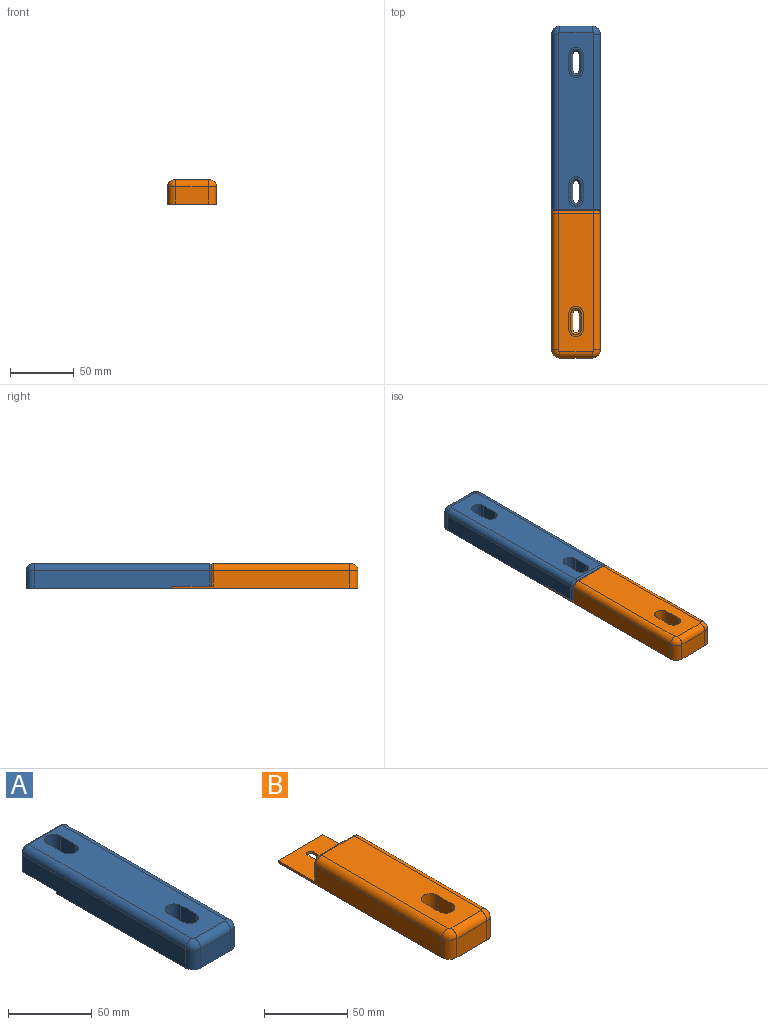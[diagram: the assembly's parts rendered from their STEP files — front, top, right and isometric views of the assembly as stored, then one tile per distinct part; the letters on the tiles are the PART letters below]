
ASSEMBLY  parts=2 mates=1
PART A: 42 faces, bbox 38.9x145.3x19.5 mm
  f0: plane 23.81x11.11mm, normal (0,0,1), area 87.8mm2, adj f16,f17,f18,f19,f26,f27,f28,f29
  f1: plane 137.32x13.97mm, normal (-1,0,0), area 1873mm2, adj f10,f11,f21,f22,f32,f41
  f2: plane 137.32x13.97mm, normal (1,0,0), area 1873mm2, adj f5,f11,f21,f22,f36,f37
  f3: plane 23.81x11.11mm, normal (0,0,1), area 87.8mm2, adj f12,f13,f14,f15,f23,f24,f25,f30
  f4: plane 25.4x13.97mm, normal (0,-1,0), area 354.8mm2, adj f5,f10,f11,f34
  f5: cylinder r=6.35mm len=13.97mm, axis (0,0,-1), area 139.3mm2, adj f2,f4,f11,f35
  f6: plane 12.7x1.59mm, normal (-1,0,0), area 20.2mm2, adj f7,f9,f11,f16
  f7: cylinder r=2.38mm len=4.76mm, axis (0,0,-1), area 11.9mm2, adj f6,f8,f11,f17
  f8: plane 12.7x1.59mm, normal (1,0,0), area 20.2mm2, adj f7,f9,f11,f19
  f9: cylinder r=2.38mm len=4.76mm, axis (0,0,-1), area 11.9mm2, adj f6,f8,f11,f18
  f10: cylinder r=6.35mm len=13.97mm, axis (0,0,-1), area 139.3mm2, adj f1,f4,f11,f33
  f11: plane 115.09x38.1mm, normal (0,0,-1), area 4289.5mm2, adj f1,f2,f4,f5,f6,f7,f8,f9
  f12: plane 12.7x1.59mm, normal (-0.71,0,0.71), area 28.5mm2, adj f3,f13,f14,f22
  f13: cone r=2.38mm half-angle=45deg, axis (0,0,1), area 22.4mm2, adj f3,f12,f15,f22
  f14: cone r=2.38mm half-angle=45deg, axis (0,0,1), area 22.4mm2, adj f3,f12,f15,f22
  f15: plane 12.7x1.59mm, normal (0.71,0,0.71), area 28.5mm2, adj f3,f13,f14,f22
  f16: plane 12.7x1.59mm, normal (-0.71,0,0.71), area 28.5mm2, adj f0,f6,f17,f18
  f17: cone r=2.38mm half-angle=45deg, axis (0,0,1), area 22.4mm2, adj f0,f7,f16,f19
  f18: cone r=2.38mm half-angle=45deg, axis (0,0,1), area 22.4mm2, adj f0,f9,f16,f19
  f19: plane 12.7x1.59mm, normal (0.71,0,0.71), area 28.5mm2, adj f0,f8,f17,f18
  f20: plane 34.93x15.88mm, normal (0,1,0), area 549.2mm2, adj f22,f37,f38,f39,f40,f41
  f21: plane 38.1x1.59mm, normal (0,1,0), area 60.5mm2, adj f1,f2,f11,f22
  f22: plane 38.1x30.16mm, normal (0,0,-1), area 1069.8mm2, adj f1,f2,f12,f13,f14,f15,f20,f21
  f23: cylinder r=5.56mm len=15.88mm, axis (0,0,-1), area 277.1mm2, adj f3,f24,f30,f31
  f24: plane 15.88x12.7mm, normal (-1,0,0), area 201.6mm2, adj f3,f23,f25,f31
  f25: cylinder r=5.56mm len=15.88mm, axis (0,0,-1), area 277.1mm2, adj f3,f24,f30,f31
  f26: cylinder r=5.56mm len=15.88mm, axis (0,0,-1), area 277.1mm2, adj f0,f27,f29,f31
  f27: plane 15.88x12.7mm, normal (-1,0,0), area 201.6mm2, adj f0,f26,f28,f31
  f28: cylinder r=5.56mm len=15.88mm, axis (0,0,-1), area 277.1mm2, adj f0,f27,f29,f31
  f29: plane 15.88x12.7mm, normal (1,0,0), area 201.6mm2, adj f0,f26,f28,f31
  f30: plane 15.88x12.7mm, normal (1,0,0), area 201.6mm2, adj f3,f23,f25,f31
  f31: plane 138.59x27.94mm, normal (0,0,1), area 3395.2mm2, adj f23,f24,f25,f26,f27,f28,f29,f30
  f32: cylinder r=5.08mm len=137.32mm, axis (0,1,0), area 1095.8mm2, adj f1,f31,f33,f40
  f33: torus R=1.27mm, axis (0,0,1), area 56.5mm2, adj f10,f31,f32,f34
  f34: cylinder r=5.08mm len=25.4mm, axis (-1,0,0), area 202.7mm2, adj f4,f31,f33,f35
  f35: torus R=1.27mm, axis (0,0,1), area 56.5mm2, adj f5,f31,f34,f36
  f36: cylinder r=5.08mm len=137.32mm, axis (0,-1,0), area 1095.8mm2, adj f2,f31,f35,f38
  f37: cylinder r=1.59mm len=12.38mm, axis (0,0,1), area 30.9mm2, adj f2,f20,f22,f38
  f38: torus R=3.49mm, axis (0,1,0), area 17.6mm2, adj f20,f36,f37,f39
  f39: cylinder r=1.59mm len=27.94mm, axis (-1,0,0), area 69.7mm2, adj f20,f31,f38,f40
  f40: torus R=3.49mm, axis (0,1,0), area 17.6mm2, adj f20,f32,f39,f41
  f41: cylinder r=1.59mm len=12.38mm, axis (0,0,-1), area 30.9mm2, adj f1,f20,f22,f40
PART B: 37 faces, bbox 38.9x145.3x19.5 mm
  f0: plane 138.91x13.97mm, normal (-1,0,0), area 1547.4mm2, adj f13,f14,f19,f21,f27,f36
  f1: plane 12.7x1.59mm, normal (-1,0,0), area 20.2mm2, adj f2,f4,f14,f21
  f2: cylinder r=2.38mm len=4.76mm, axis (0,0,-1), area 11.9mm2, adj f1,f3,f14,f21
  f3: plane 12.7x1.59mm, normal (1,0,0), area 20.2mm2, adj f2,f4,f14,f21
  f4: cylinder r=2.38mm len=4.76mm, axis (0,0,-1), area 11.9mm2, adj f1,f3,f14,f21
  f5: plane 138.91x13.97mm, normal (1,0,0), area 1547.4mm2, adj f8,f14,f19,f21,f31,f32
  f6: plane 23.81x11.11mm, normal (0,0,1), area 87.8mm2, adj f15,f16,f17,f18,f22,f23,f24,f25
  f7: plane 25.4x13.97mm, normal (0,-1,0), area 354.8mm2, adj f8,f13,f14,f29
  f8: cylinder r=6.35mm len=13.97mm, axis (0,0,-1), area 139.3mm2, adj f5,f7,f14,f30
  f9: plane 12.7x1.59mm, normal (-1,0,0), area 20.2mm2, adj f10,f12,f14,f15
  f10: cylinder r=2.38mm len=4.76mm, axis (0,0,-1), area 11.9mm2, adj f9,f11,f14,f16
  f11: plane 12.7x1.59mm, normal (1,0,0), area 20.2mm2, adj f10,f12,f14,f18
  f12: cylinder r=2.38mm len=4.76mm, axis (0,0,-1), area 11.9mm2, adj f9,f11,f14,f17
  f13: cylinder r=6.35mm len=13.97mm, axis (0,0,-1), area 139.3mm2, adj f0,f7,f14,f28
  f14: plane 145.26x38.1mm, normal (0,0,-1), area 5360.4mm2, adj f0,f1,f2,f3,f4,f5,f7,f8
  f15: plane 12.7x1.59mm, normal (-0.71,0,0.71), area 28.5mm2, adj f6,f9,f16,f17
  f16: cone r=2.38mm half-angle=45deg, axis (0,0,1), area 22.4mm2, adj f6,f10,f15,f18
  f17: cone r=2.38mm half-angle=45deg, axis (0,0,1), area 22.4mm2, adj f6,f12,f15,f18
  f18: plane 12.7x1.59mm, normal (0.71,0,0.71), area 28.5mm2, adj f6,f11,f16,f17
  f19: plane 38.1x1.59mm, normal (0,1,0), area 60.5mm2, adj f0,f5,f14,f21
  f20: plane 34.93x15.88mm, normal (0,1,0), area 549.2mm2, adj f21,f32,f33,f34,f35,f36
  f21: plane 38.1x31.75mm, normal (0,0,1), area 1072mm2, adj f0,f1,f2,f3,f4,f5,f19,f20
  f22: cylinder r=5.56mm len=15.88mm, axis (0,0,-1), area 277.1mm2, adj f6,f23,f25,f26
  f23: plane 15.88x12.7mm, normal (-1,0,0), area 201.6mm2, adj f6,f22,f24,f26
  f24: cylinder r=5.56mm len=15.88mm, axis (0,0,-1), area 277.1mm2, adj f6,f23,f25,f26
  f25: plane 15.88x12.7mm, normal (1,0,0), area 201.6mm2, adj f6,f22,f24,f26
  f26: plane 108.43x27.94mm, normal (0,0,1), area 2790.6mm2, adj f22,f23,f24,f25,f27,f28,f29,f30
  f27: cylinder r=5.08mm len=107.16mm, axis (0,1,0), area 855.1mm2, adj f0,f26,f28,f35
  f28: torus R=1.27mm, axis (0,0,1), area 56.5mm2, adj f13,f26,f27,f29
  f29: cylinder r=5.08mm len=25.4mm, axis (-1,0,0), area 202.7mm2, adj f7,f26,f28,f30
  f30: torus R=1.27mm, axis (0,0,1), area 56.5mm2, adj f8,f26,f29,f31
  f31: cylinder r=5.08mm len=107.16mm, axis (0,-1,0), area 855.1mm2, adj f5,f26,f30,f33
  f32: cylinder r=1.59mm len=12.38mm, axis (0,0,1), area 30.9mm2, adj f5,f20,f21,f33
  f33: torus R=3.49mm, axis (0,-1,0), area 17.6mm2, adj f20,f31,f32,f34
  f34: cylinder r=1.59mm len=27.94mm, axis (-1,0,0), area 69.7mm2, adj f20,f26,f33,f35
  f35: torus R=3.49mm, axis (0,-1,0), area 17.6mm2, adj f20,f27,f34,f36
  f36: cylinder r=1.59mm len=12.38mm, axis (0,0,-1), area 30.9mm2, adj f0,f20,f21,f35
PLACE A rot(axis=(0,0,1),180deg) t=(38.1,260.35,0)mm
PLACE B at identity
MATE fastened A.f22 <-> B.f21  axis (0,0,-1) through (19.05,130.18,1.59)mm
